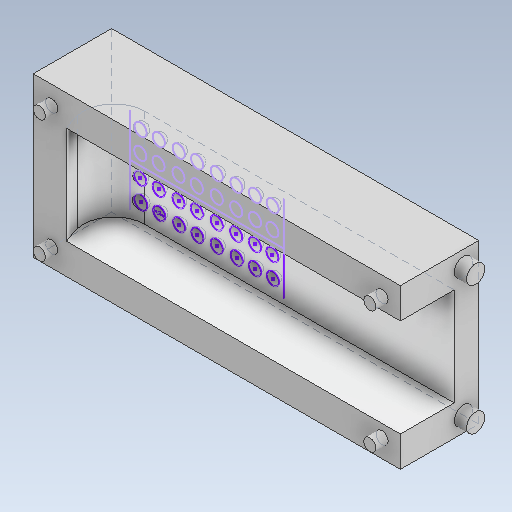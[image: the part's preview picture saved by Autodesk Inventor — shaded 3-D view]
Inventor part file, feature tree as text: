
AUTODESK INVENTOR PART (.ipt)
format: ipt  version: 2025.2 (Build 292293000, 293)  size: 602,112 bytes
history: native  units: mm
features: sketch x36, revolve x32, other x4, extrude x4
ambient origin geometry x8: Origin, YZ Plane, XZ Plane, XY Plane, X Axis, Y Axis, Z Axis, Center Point
bodies: Volumenkörper5 (feature_tree), Solid2 (feature_tree)
feature tree (76):
  other  "Maria_Greifer_Finger_beide_Seiten - KopieVorlageForm.ipt"
  extrude  "Extrusion5"  Depth=10.0mm TaperAngle=0.0deg
  other  "Kombinieren2"
  extrude  "Extrusion6"  Depth=5.0mm
  sketch  "Skizze7"  dims[d27=5.0mm d28=4.0mm]
  revolve  "Umdrehung1"
  revolve  "Umdrehung2"
  revolve  "Umdrehung4"
  revolve  "Umdrehung6"
  revolve  "Umdrehung7"
  revolve  "Umdrehung8"
  revolve  "Umdrehung9"
  revolve  "Umdrehung10"
  revolve  "Umdrehung11"
  revolve  "Umdrehung12"
  revolve  "Umdrehung13"
  revolve  "Umdrehung14"
  revolve  "Umdrehung15"
  revolve  "Umdrehung16"
  revolve  "Umdrehung17"
  revolve  "Umdrehung18"
  revolve  "Umdrehung19"
  revolve  "Umdrehung20"
  revolve  "Umdrehung21"
  revolve  "Umdrehung22"
  revolve  "Umdrehung23"
  revolve  "Umdrehung24"
  revolve  "Umdrehung25"
  revolve  "Umdrehung26"
  revolve  "Umdrehung27"
  revolve  "Umdrehung28"
  revolve  "Umdrehung29"
  revolve  "Umdrehung30"
  revolve  "Umdrehung31"
  revolve  "Umdrehung32"
  extrude  "Extrusion7"  Depth=5.0mm
  extrude  "Extrusion8"  Depth=25.6mm
  revolve  "Umdrehung36"
  revolve  "Umdrehung37"
  other  "Solid2::Maria_Greifer_Finger_beide_Seiten - KopieVorlageForm.ipt"
  other  "Bezeichnung3"
  sketch  "Skizze5"  dims[d22=10.0mm d23=60.0mm d24=0.0mm]
  sketch  "Skizze6"  dims[d25=5.0mm d26=4.0mm]
  sketch  "Skizze8"  dims[d29=60.0mm d30=0.0mm d31=25.6mm]
  sketch  "Skizze10"  dims[d32=12.8mm]
  sketch  "Skizze12"  dims[d33=360.0deg]
  sketch  "Skizze13"  dims[d34=360.0deg]
  sketch  "Skizze14"  dims[d36=360.0deg]
  sketch  "Skizze15"  dims[d38=360.0deg]
  sketch  "Skizze16"  dims[d39=360.0deg]
  sketch  "Skizze17"  dims[d40=360.0deg]
  sketch  "Skizze18"  dims[d41=360.0deg]
  sketch  "Skizze19"  dims[d42=360.0deg]
  sketch  "Skizze20"  dims[d43=360.0deg]
  sketch  "Skizze21"  dims[d44=360.0deg]
  sketch  "Skizze22"  dims[d45=360.0deg]
  sketch  "Skizze23"  dims[d46=360.0deg]
  sketch  "Skizze24"  dims[d47=360.0deg]
  sketch  "Skizze25"  dims[d48=360.0deg]
  sketch  "Skizze26"  dims[d49=360.0deg]
  sketch  "Skizze27"  dims[d50=360.0deg]
  sketch  "Skizze28"  dims[d51=360.0deg]
  sketch  "Skizze29"  dims[d52=360.0deg]
  sketch  "Skizze30"  dims[d53=360.0deg]
  sketch  "Skizze31"  dims[d54=360.0deg]
  sketch  "Skizze32"  dims[d55=360.0deg]
  sketch  "Skizze33"  dims[d56=360.0deg]
  sketch  "Skizze34"  dims[d57=360.0deg]
  sketch  "Skizze35"  dims[d58=360.0deg]
  sketch  "Skizze36"  dims[d59=360.0deg]
  sketch  "Skizze37"  dims[d60=360.0deg]
  sketch  "Skizze38"  dims[d61=360.0deg]
  sketch  "Skizze39"  dims[d62=360.0deg]
  sketch  "Skizze40"  dims[d63=360.0deg]
  sketch  "Skizze43"  dims[d64=360.0deg]
  sketch  "Skizze44"  dims[d65=2.0mm d66=3.0mm d67=3.0mm d69=2.0mm d70=3.0mm d71=3.0mm d72=2.0mm d73=3.0mm d74=3.0mm d75=2.0mm d76=3.0mm d77=3.0mm d78=2.0mm d79=0.0mm d80=3.0mm d81=2.5mm d82=2.5mm d83=3.0mm d84=2.5mm d85=2.5mm d86=2.0mm d87=0.0mm d89=12.8mm d92=360.0deg d93=360.0deg d12=0.5mm d13=0.872665mm d14=0.5mm d15=0.872665mm]
